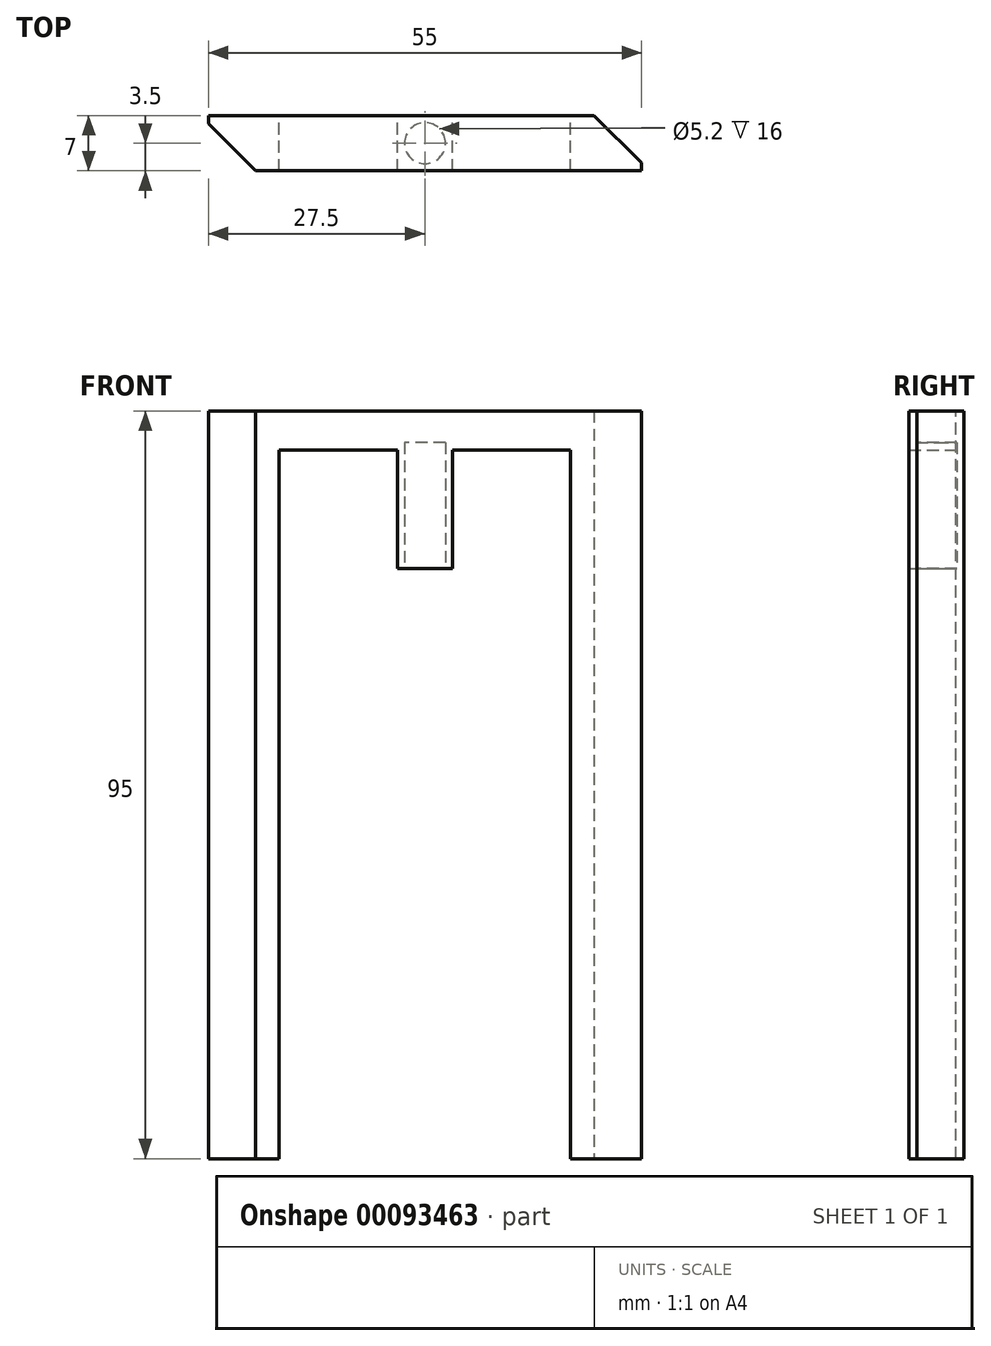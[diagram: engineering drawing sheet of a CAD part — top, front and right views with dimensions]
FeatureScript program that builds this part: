
annotation { "Feature Type Name" : "Feature", "Feature Type Description" : "" }
export const myFeature = defineFeature(function(context is Context, id is Id, definition is map)
    precondition{}
    {
        {
            var Q0;
            Q0=qCreatedBy(makeId("Front.planeOp"),FACE);
            var sketch = newSketch(context, id + "F0", { "sketchPlane" : qUnion([Q0])});
            skLineSegment(sketch, "E0.rect.bottom", {"start": v(-3.5, 0) * mm, "end": v(3.5, 0) * mm});
            skLineSegment(sketch, "E0.rect.top", {"start": v(-3.5, 20) * mm, "end": v(3.5, 20) * mm});
            skLineSegment(sketch, "E0.rect.left", {"start": v(-3.5, 0) * mm, "end": v(-3.5, 20) * mm});
            skLineSegment(sketch, "E0.rect.right", {"start": v(3.5, 0) * mm, "end": v(3.5, 20) * mm});
            skPoint(sketch, "E0.rect.middle", {"position": v(0, 10) * mm});
            skLineSegment(sketch, "E1.bottom", {"start": v(3.5, 20) * mm, "end": v(-27.5, 20) * mm});
            skLineSegment(sketch, "E1.top", {"start": v(3.5, 15) * mm, "end": v(-27.5, 15) * mm});
            skLineSegment(sketch, "E1.left", {"start": v(3.5, 20) * mm, "end": v(3.5, 15) * mm});
            skLineSegment(sketch, "E1.right", {"start": v(-27.5, 20) * mm, "end": v(-27.5, 15) * mm});
            skLineSegment(sketch, "E2.bottom", {"start": v(-27.5, 20) * mm, "end": v(-18.5, 20) * mm});
            skLineSegment(sketch, "E2.top", {"start": v(-27.5, -75) * mm, "end": v(-18.5, -75) * mm});
            skLineSegment(sketch, "E2.left", {"start": v(-27.5, 20) * mm, "end": v(-27.5, -75) * mm});
            skLineSegment(sketch, "E2.right", {"start": v(-18.5, 20) * mm, "end": v(-18.5, -75) * mm});
            skSolve(sketch);
        }
        {
            var Q0;
            Q0=qSketchRegion(id+"F0",true);
            extrude(context, id + "F1", {"entities" : qUnion([Q0]), "depth" : 7 * mm});
        }
        {
            var Q0;
            Q0=makeQuery(id+"F1.opExtrude","SWEPT_BODY",BODY,{"disambiguationData":[OSD([sQuery(id+"F0.wireOp",EDGE,"E0.rect.bottom"),sQuery(id+"F0.wireOp",EDGE,"E0.rect.left"),sQuery(id+"F0.wireOp",EDGE,"E0.rect.right"),sQuery(id+"F0.wireOp",EDGE,"E1.bottom"),sQuery(id+"F0.wireOp",EDGE,"E1.top"),sQuery(id+"F0.wireOp",EDGE,"E1.left"),sQuery(id+"F0.wireOp",EDGE,"E2.bottom"),sQuery(id+"F0.wireOp",EDGE,"E2.left"),sQuery(id+"F0.wireOp",EDGE,"E2.right"),sQuery(id+"F0.wireOp",EDGE,"443210d0-4ed6-43cc-b061-75901669d9c0.rect.bottom"),sQuery(id+"F0.wireOp",EDGE,"443210d0-4ed6-43cc-b061-75901669d9c0.rect.top"),sQuery(id+"F0.wireOp",EDGE,"443210d0-4ed6-43cc-b061-75901669d9c0.rect.left"),sQuery(id+"F0.wireOp",EDGE,"443210d0-4ed6-43cc-b061-75901669d9c0.rect.right")])]});
            var Q1;
            Q1=qCreatedBy(makeId("Right.planeOp"),FACE);
            mirror(context, id + "F2", {"operationType" : NewBodyOperationType.ADD, "entities" : qUnion([Q0]), "mirrorPlane" : qUnion([Q1])});
        }
        {
            var Q0;
            Q0=qCreatedBy(makeId("Top.planeOp"),FACE);
            var sketch = newSketch(context, id + "F3", { "sketchPlane" : qUnion([Q0])});
            skCircle(sketch, "E3", {"center": v(0, -3.5) * mm, "radius": 2.6 * mm});
            skSolve(sketch);
        }
        {
            var Q0;
            Q0=makeQuery(id+"F3.imprint","IMPRINT",FACE,{"disambiguationData":[TD([[makeQuery(id+"F3.imprint","IMPRINT",EDGE,{"derivedFrom":sQuery(id+"F3.wireOp",EDGE,"E3")}),1.0]])]});
            extrude(context, id + "F4", {"entities" : qUnion([Q0]), "operationType" : NewBodyOperationType.REMOVE, "depth" : 16 * mm});
        }
        {
            var Q0;
            Q0=makeQuery(id+"F1.opExtrude","CAP_EDGE",EDGE,{"disambiguationData":[OSD([sQuery(id+"F0.wireOp",EDGE,"E2.left")])],"isStart":false});
            chamfer(context, id + "F5", {"entities" : qUnion([Q0]), "width" : 6 * mm, "tangentPropagation" : true});
        }
        {
            var Q0;
            Q0=makeQuery(id+"F2.opPattern","COPY",EDGE,{"derivedFrom":makeQuery(id+"F1.opExtrude","CAP_EDGE",EDGE,{"disambiguationData":[OSD([sQuery(id+"F0.wireOp",EDGE,"E2.left")])],"isStart":true}),"instanceName":"1"});
            chamfer(context, id + "F6", {"entities" : qUnion([Q0]), "width" : 6 * mm, "tangentPropagation" : true});
        }
    });
